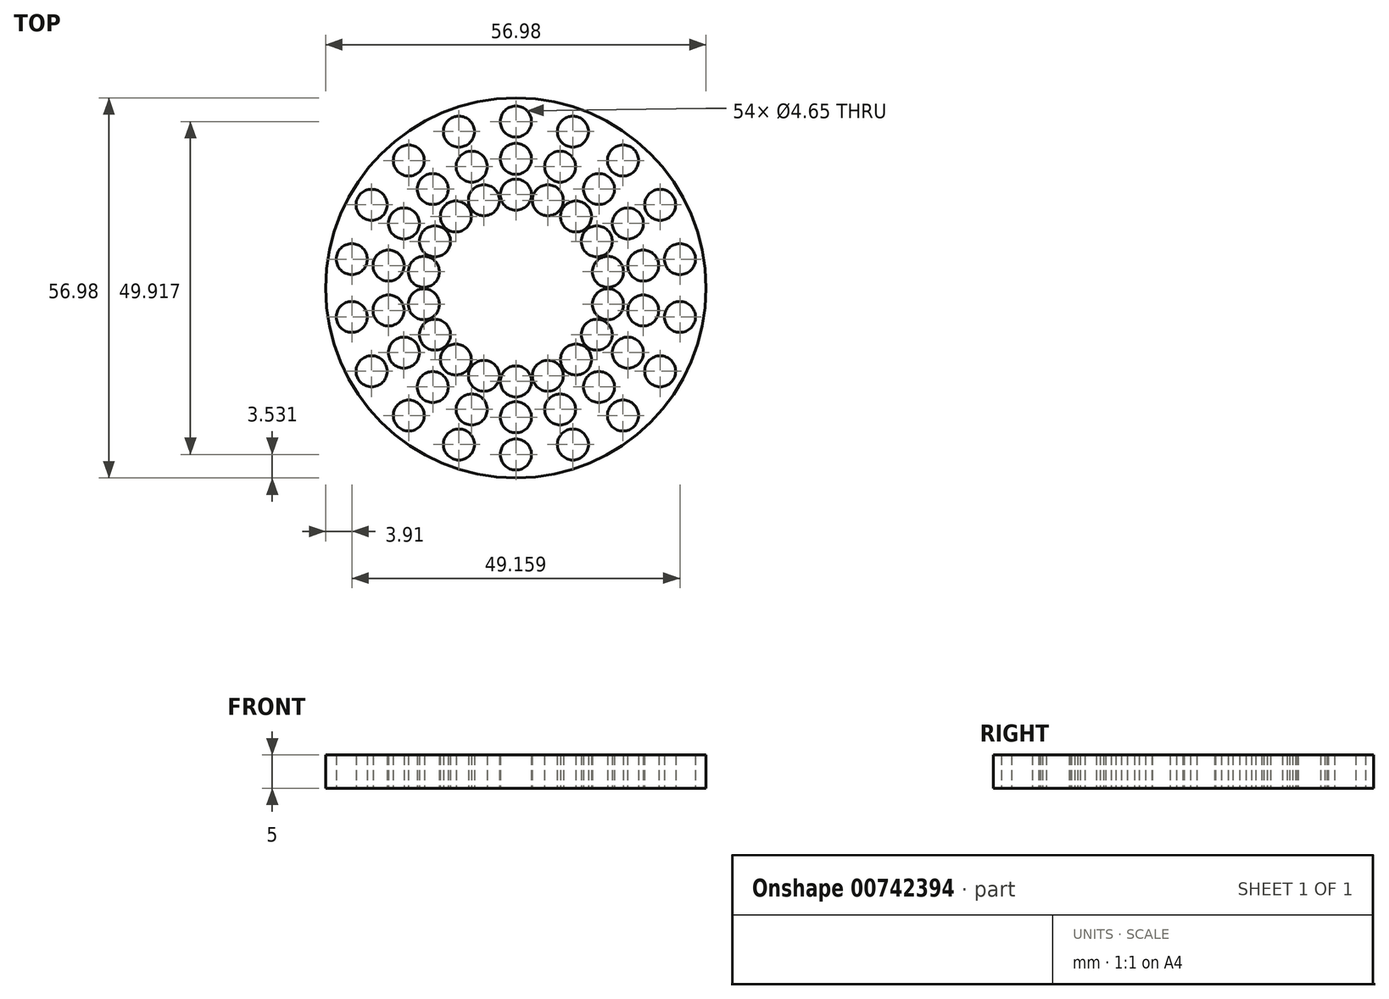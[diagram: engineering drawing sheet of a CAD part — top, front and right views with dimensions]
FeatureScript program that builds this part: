
annotation { "Feature Type Name" : "Feature", "Feature Type Description" : "" }
export const myFeature = defineFeature(function(context is Context, id is Id, definition is map)
    precondition{}
    {
        {
            var Q0;
            Q0=qCreatedBy(makeId("Top.planeOp"),FACE);
            var sketch = newSketch(context, id + "F0", { "sketchPlane" : qUnion([Q0])});
            skCircle(sketch, "E0", {"center": v(0, 0) * mm, "radius": 14 * mm});
            skCircle(sketch, "E1", {"center": v(0, 0) * mm, "radius": 28.49 * mm});
            skCircle(sketch, "E2", {"center": v(0, 24.96) * mm, "radius": 2.33 * mm});
            skCircle(sketch, "E3", {"center": v(0, 19.37) * mm, "radius": 2.33 * mm});
            skCircle(sketch, "E4", {"center": v(0, 14) * mm, "radius": 2.33 * mm});
            skCircle(sketch, "E5.1.0", {"center": v(-4.79, 13.16) * mm, "radius": 2.33 * mm});
            skCircle(sketch, "E5.1.1", {"center": v(-8.54, 23.45) * mm, "radius": 2.33 * mm});
            skCircle(sketch, "E5.1.2", {"center": v(-6.62, 18.2) * mm, "radius": 2.33 * mm});
            skCircle(sketch, "E5.2.0", {"center": v(-9, 10.72) * mm, "radius": 2.32 * mm});
            skCircle(sketch, "E5.2.1", {"center": v(-16.04, 19.12) * mm, "radius": 2.32 * mm});
            skCircle(sketch, "E5.2.2", {"center": v(-12.45, 14.84) * mm, "radius": 2.32 * mm});
            skCircle(sketch, "E5.3.0", {"center": v(-12.12, 7) * mm, "radius": 2.33 * mm});
            skCircle(sketch, "E5.3.1", {"center": v(-21.61, 12.48) * mm, "radius": 2.33 * mm});
            skCircle(sketch, "E5.3.2", {"center": v(-16.77, 9.68) * mm, "radius": 2.33 * mm});
            skCircle(sketch, "E5.4.0", {"center": v(-13.79, 2.43) * mm, "radius": 2.32 * mm});
            skCircle(sketch, "E5.4.1", {"center": v(-24.58, 4.33) * mm, "radius": 2.32 * mm});
            skCircle(sketch, "E5.4.2", {"center": v(-19.08, 3.36) * mm, "radius": 2.32 * mm});
            skCircle(sketch, "E5.5.0", {"center": v(-13.79, -2.43) * mm, "radius": 2.32 * mm});
            skCircle(sketch, "E5.5.1", {"center": v(-24.58, -4.33) * mm, "radius": 2.32 * mm});
            skCircle(sketch, "E5.5.2", {"center": v(-19.08, -3.36) * mm, "radius": 2.32 * mm});
            skCircle(sketch, "E5.6.0", {"center": v(-12.12, -7) * mm, "radius": 2.32 * mm});
            skCircle(sketch, "E5.6.1", {"center": v(-21.61, -12.48) * mm, "radius": 2.32 * mm});
            skCircle(sketch, "E5.6.2", {"center": v(-16.77, -9.68) * mm, "radius": 2.32 * mm});
            skCircle(sketch, "E5.7.0", {"center": v(-9, -10.72) * mm, "radius": 2.32 * mm});
            skCircle(sketch, "E5.7.1", {"center": v(-16.04, -19.12) * mm, "radius": 2.32 * mm});
            skCircle(sketch, "E5.7.2", {"center": v(-12.45, -14.84) * mm, "radius": 2.32 * mm});
            skCircle(sketch, "E5.8.0", {"center": v(-4.79, -13.16) * mm, "radius": 2.32 * mm});
            skCircle(sketch, "E5.8.1", {"center": v(-8.54, -23.45) * mm, "radius": 2.32 * mm});
            skCircle(sketch, "E5.8.2", {"center": v(-6.62, -18.2) * mm, "radius": 2.32 * mm});
            skCircle(sketch, "E5.9.0", {"center": v(0, -14) * mm, "radius": 2.33 * mm});
            skCircle(sketch, "E5.9.1", {"center": v(0, -24.96) * mm, "radius": 2.33 * mm});
            skCircle(sketch, "E5.9.2", {"center": v(0, -19.37) * mm, "radius": 2.33 * mm});
            skCircle(sketch, "E6.1.10.0", {"center": v(4.79, -13.16) * mm, "radius": 2.33 * mm});
            skCircle(sketch, "E6.2.10.0", {"center": v(8.54, -23.45) * mm, "radius": 2.33 * mm});
            skCircle(sketch, "E6.4.10.0", {"center": v(6.62, -18.2) * mm, "radius": 2.33 * mm});
            skCircle(sketch, "E7.1.11.0", {"center": v(9, -10.72) * mm, "radius": 2.33 * mm});
            skCircle(sketch, "E7.2.11.0", {"center": v(16.04, -19.12) * mm, "radius": 2.33 * mm});
            skCircle(sketch, "E7.4.11.0", {"center": v(12.45, -14.84) * mm, "radius": 2.33 * mm});
            skCircle(sketch, "E8.1.12.0", {"center": v(12.12, -7) * mm, "radius": 2.32 * mm});
            skCircle(sketch, "E8.2.12.0", {"center": v(21.61, -12.48) * mm, "radius": 2.32 * mm});
            skCircle(sketch, "E8.4.12.0", {"center": v(16.77, -9.68) * mm, "radius": 2.32 * mm});
            skCircle(sketch, "E8.1.13.0", {"center": v(13.79, -2.43) * mm, "radius": 2.32 * mm});
            skCircle(sketch, "E8.2.13.0", {"center": v(24.58, -4.33) * mm, "radius": 2.32 * mm});
            skCircle(sketch, "E8.4.13.0", {"center": v(19.08, -3.36) * mm, "radius": 2.32 * mm});
            skCircle(sketch, "E9.1.14.0", {"center": v(13.79, 2.43) * mm, "radius": 2.33 * mm});
            skCircle(sketch, "E9.2.14.0", {"center": v(24.58, 4.33) * mm, "radius": 2.33 * mm});
            skCircle(sketch, "E9.4.14.0", {"center": v(19.08, 3.36) * mm, "radius": 2.33 * mm});
            skCircle(sketch, "E9.1.15.0", {"center": v(12.12, 7) * mm, "radius": 2.33 * mm});
            skCircle(sketch, "E9.2.15.0", {"center": v(21.61, 12.48) * mm, "radius": 2.33 * mm});
            skCircle(sketch, "E9.4.15.0", {"center": v(16.77, 9.68) * mm, "radius": 2.33 * mm});
            skCircle(sketch, "E10.1.16.0", {"center": v(9, 10.72) * mm, "radius": 2.33 * mm});
            skCircle(sketch, "E10.2.16.0", {"center": v(16.04, 19.12) * mm, "radius": 2.33 * mm});
            skCircle(sketch, "E10.4.16.0", {"center": v(12.45, 14.84) * mm, "radius": 2.33 * mm});
            skCircle(sketch, "E10.1.17.0", {"center": v(4.79, 13.16) * mm, "radius": 2.33 * mm});
            skCircle(sketch, "E10.2.17.0", {"center": v(8.54, 23.45) * mm, "radius": 2.33 * mm});
            skCircle(sketch, "E10.4.17.0", {"center": v(6.62, 18.2) * mm, "radius": 2.33 * mm});
            skSolve(sketch);
        }
        {
            var Q0;
            Q0=makeQuery(id+"F0.imprint","IMPRINT",FACE,{"disambiguationData":[TD([[makeQuery(id+"F0.imprint","IMPRINT",EDGE,{"derivedFrom":sQuery(id+"F0.wireOp",EDGE,"E1")}),1.0]])]});
            var Q1;
            {var subQ1=sQuery(id+"F0.wireOp",EDGE,"E0");var subQ10=sQuery(id+"F0.wireOp",EDGE,"E9.1.14.0");var subQ47=makeQuery(id+"F0.imprint","INTERSECT",VERTEX,{"disambiguationData":[OD(0.0)],"derivedFrom":[subQ1,subQ10]});Q1=makeQuery(id+"F0.imprint","IMPRINT",FACE,{"disambiguationData":[TD([[makeQuery(id+"F0.imprint","IMPRINT",EDGE,{"disambiguationData":[TD([[subQ47,-1.0]])],"derivedFrom":subQ1}),1.0]])]});}
            extrude(context, id + "F1", {"entities" : qUnion([Q0, Q1]), "depth" : 5 * mm, "offsetDistance" : 25 * mm});
        }
    });
